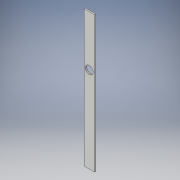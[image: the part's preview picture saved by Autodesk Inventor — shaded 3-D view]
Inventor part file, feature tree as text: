
AUTODESK INVENTOR PART (.ipt)
format: ipt  version: 2018 (Build 220112000, 112)  size: 97,792 bytes
history: native  units: in
note: dims shown in document units (in); Inventor stores cm internally (conversion verified against a paired STEP export)
features: extrude x1, sketch x1
ambient origin geometry x8: Origin, YZ Plane, XZ Plane, XY Plane, X Axis, Y Axis, Z Axis, Center Point
bodies: Solid1 (feature_tree)
feature tree (2):
  extrude  "Extrusion1"  Depth=13.0in
  sketch  "Sketch1"  dims[d0=1.0in d1=13.0in d2=8.1875in d3=0.75in d4=0.125in d5=0.0in]
